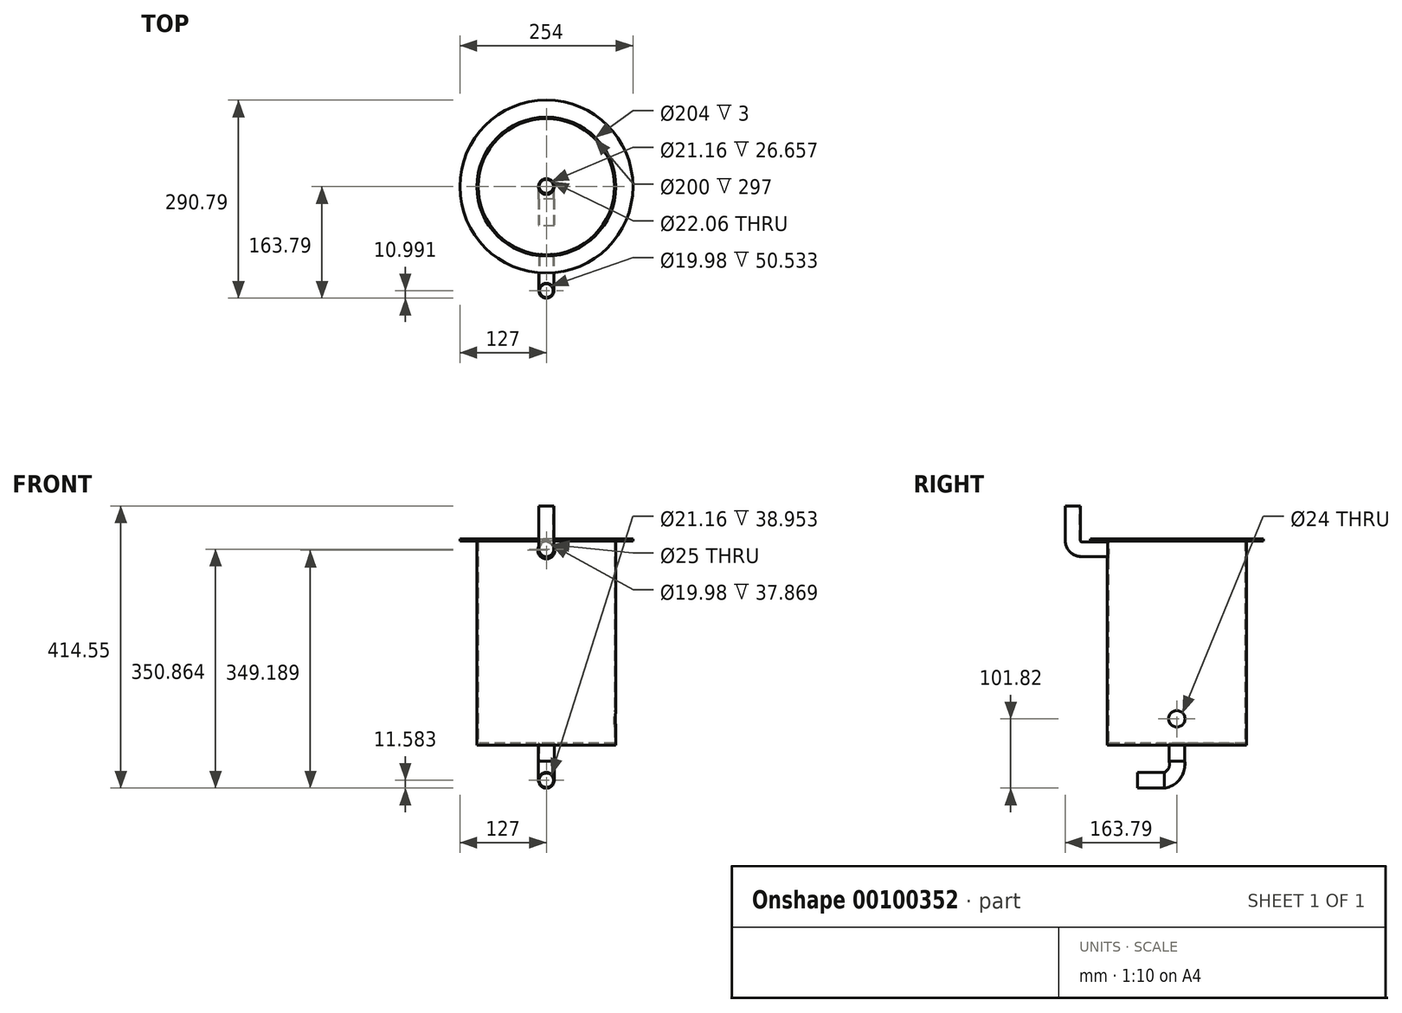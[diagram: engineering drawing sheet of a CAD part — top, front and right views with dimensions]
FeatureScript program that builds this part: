
annotation { "Feature Type Name" : "Feature", "Feature Type Description" : "" }
export const myFeature = defineFeature(function(context is Context, id is Id, definition is map)
    precondition{}
    {
        {
            var Q0;
            Q0=qCreatedBy(makeId("Top.planeOp"),FACE);
            var sketch = newSketch(context, id + "F0", { "sketchPlane" : qUnion([Q0])});
            skCircle(sketch, "E0", {"center": v(0, 0) * mm, "radius": 100 * mm});
            skCircle(sketch, "E1", {"center": v(0, 0) * mm, "radius": 102 * mm});
            skCircle(sketch, "E2", {"center": v(0, 0) * mm, "radius": 11.03 * mm});
            skSolve(sketch);
        }
        {
            var Q0;
            Q0=makeQuery(id+"F0.imprint","IMPRINT",FACE,{"disambiguationData":[TD([[makeQuery(id+"F0.imprint","IMPRINT",EDGE,{"derivedFrom":sQuery(id+"F0.wireOp",EDGE,"E0")}),-1.0]])]});
            extrude(context, id + "F1", {"entities" : qUnion([Q0]), "depth" : 300 * mm});
        }
        {
            var Q0;
            Q0=makeQuery(id+"F1.opExtrude","CAP_FACE",FACE,{"disambiguationData":[OSD([sQuery(id+"F0.wireOp",EDGE,"E0"),sQuery(id+"F0.wireOp",EDGE,"E1")])],"isStart":false});
            var sketch = newSketch(context, id + "F2", { "sketchPlane" : qUnion([Q0])});
            skCircle(sketch, "E3", {"center": v(0, 0) * mm, "radius": 102 * mm});
            skCircle(sketch, "E4", {"center": v(0, 0) * mm, "radius": 127 * mm});
            skSolve(sketch);
        }
        {
            var Q0;
            Q0=makeQuery(id+"F2.imprint","IMPRINT",FACE,{"disambiguationData":[TD([[makeQuery(id+"F2.imprint","IMPRINT",EDGE,{"derivedFrom":sQuery(id+"F2.wireOp",EDGE,"E4")}),1.0]])]});
            var Q1;
            Q1=makeQuery(id+"F2.imprint","IMPRINT",FACE,{"disambiguationData":[TD([[makeQuery(id+"F2.imprint","IMPRINT",EDGE,{"derivedFrom":sQuery(id+"F2.wireOp",EDGE,"E3")}),-1.0]])]});
            extrude(context, id + "F3", {"entities" : qUnion([Q0, Q1]), "depth" : 3 * mm});
        }
        {
            var Q0;
            Q0=qCreatedBy(makeId("Right.planeOp"),FACE);
            cPlane(context, id + "F4", {"entities" : qUnion([Q0]), "cplaneType" : CPlaneType.OFFSET, "offset" : 97 * mm, "width" : 152.4 * mm, "height" : 152.4 * mm});
        }
        {
            var Q0;
            Q0=qCreatedBy(id+"F4.planeOp",FACE);
            var sketch = newSketch(context, id + "F5", { "sketchPlane" : qUnion([Q0])});
            skPoint(sketch, "E5", {"position": v(0, 38.72) * mm});
            skSolve(sketch);
        }
        {
            var Q0;
            Q0=makeQuery(id+"F0.imprint","IMPRINT",FACE,{"disambiguationData":[TD([[makeQuery(id+"F0.imprint","IMPRINT",EDGE,{"derivedFrom":sQuery(id+"F0.wireOp",EDGE,"E0")}),1.0]])]});
            extrude(context, id + "F6", {"entities" : qUnion([Q0]), "operationType" : NewBodyOperationType.ADD, "depth" : 3 * mm});
        }
        {
            var Q0;
            Q0=sQuery(id+"F5.wireOp",VERTEX,"E5");
            var Q1;
            Q1=makeQuery(id+"F1.opExtrude","SWEPT_BODY",BODY,{"disambiguationData":[OSD([sQuery(id+"F0.wireOp",EDGE,"E0"),sQuery(id+"F0.wireOp",EDGE,"E1")])]});
            hole(context, id + "F7", {"style" : HoleStyle.SIMPLE, "endStyle" : HoleEndStyle.BLIND, "oppositeDirection" : true, "holeDiameter" : 24 * mm, "holeDepth" : 30 * mm, "startFromSketch" : true, "locations" : qUnion([Q0]), "scope" : qUnion([Q1])});
        }
        {
            var Q0;
            Q0=qCreatedBy(makeId("Front.planeOp"),FACE);
            cPlane(context, id + "F8", {"entities" : qUnion([Q0]), "cplaneType" : CPlaneType.OFFSET, "offset" : 102 * mm, "width" : 150 * mm, "height" : 150 * mm});
        }
        {
            var Q0;
            Q0=qCreatedBy(id+"F8.planeOp",FACE);
            var sketch = newSketch(context, id + "F9", { "sketchPlane" : qUnion([Q0])});
            skPoint(sketch, "E6", {"position": v(0, 286.09) * mm});
            skSolve(sketch);
        }
        {
            var Q0;
            Q0=sQuery(id+"F9.wireOp",VERTEX,"E6");
            var Q1;
            Q1=makeQuery(id+"F1.opExtrude","SWEPT_BODY",BODY,{"disambiguationData":[OSD([sQuery(id+"F0.wireOp",EDGE,"E0"),sQuery(id+"F0.wireOp",EDGE,"E1")])]});
            hole(context, id + "F10", {"style" : HoleStyle.SIMPLE, "endStyle" : HoleEndStyle.BLIND, "holeDiameter" : 25 * mm, "holeDepth" : 40 * mm, "locations" : qUnion([Q0]), "scope" : qUnion([Q1])});
        }
        {
            var Q0;
            Q0=qCreatedBy(makeId("Right.planeOp"),FACE);
            var sketch = newSketch(context, id + "F11", { "sketchPlane" : qUnion([Q0])});
            skLineSegment(sketch, "E7", {"start": v(-101.77, 287.76) * mm, "end": v(-139.64, 287.76) * mm});
            skArc(sketch, "E8", {"start": v(-139.64, 287.76) * mm, "mid": v(-148.94, 291.62) * mm, "end": v(-152.8, 300.92) * mm});
            skLineSegment(sketch, "E9", {"start": v(-152.8, 300.92) * mm, "end": v(-152.8, 351.45) * mm});
            skSolve(sketch);
        }
        {
            var Q0;
            Q0=qCreatedBy(id+"F8.planeOp",FACE);
            var sketch = newSketch(context, id + "F12", { "sketchPlane" : qUnion([Q0])});
            skCircle(sketch, "E10", {"center": v(0, 287.76) * mm, "radius": 10.99 * mm});
            skCircle(sketch, "E11.0", {"center": v(0, 287.76) * mm, "radius": 9.99 * mm});
            skSolve(sketch);
        }
        {
            var Q0;
            Q0 = qSketchRegion(id + "F12", true);
            var Q1;
            Q1 = qConstructionFilter(qBodyType(qCreatedBy(id + "F11" ,EDGE), BodyType.WIRE), ConstructionObject.NO);
            sweep(context, id + "F13", {"profiles" : qUnion([Q0]), "path" : qUnion([Q1])});
        }
        {
            var Q0;
            Q0=qCreatedBy(makeId("Right.planeOp"),FACE);
            var sketch = newSketch(context, id + "F14", { "sketchPlane" : qUnion([Q0])});
            skArc(sketch, "E12", {"start": v(-0.12, -28.32) * mm, "mid": v(-6.88, -44.64) * mm, "end": v(-23.2, -51.4) * mm});
            skLineSegment(sketch, "E13", {"start": v(-23.2, -51.4) * mm, "end": v(-62.15, -51.4) * mm});
            skLineSegment(sketch, "E14", {"start": v(-0.12, -28.32) * mm, "end": v(-0.12, -1.66) * mm});
            skSolve(sketch);
        }
        {
            var Q0;
            Q0=makeQuery(id+"F6.opExtrude","CAP_FACE",FACE,{"disambiguationData":[OSD([sQuery(id+"F0.wireOp",EDGE,"E0"),sQuery(id+"F0.wireOp",EDGE,"E2")])],"isStart":false});
            var sketch = newSketch(context, id + "F15", { "sketchPlane" : qUnion([Q0])});
            skCircle(sketch, "E15", {"center": v(0, 0) * mm, "radius": 10.58 * mm});
            skCircle(sketch, "E16.0", {"center": v(0, 0) * mm, "radius": 11.58 * mm});
            skSolve(sketch);
        }
        {
            var Q0;
            Q0 = qSketchRegion(id + "F15", true);
            var Q1;
            Q1 = qConstructionFilter(qBodyType(qCreatedBy(id + "F14" ,EDGE), BodyType.WIRE), ConstructionObject.NO);
            sweep(context, id + "F16", {"profiles" : qUnion([Q0]), "path" : qUnion([Q1])});
        }
        {
            var Q0;
            Q0=qCreatedBy(id+"F4.planeOp",FACE);
            var sketch = newSketch(context, id + "F17", { "sketchPlane" : qUnion([Q0])});
            skCircle(sketch, "E17", {"center": v(0, 39) * mm, "radius": 11 * mm});
            skSolve(sketch);
        }
        {
            var Q0;
            Q0=sQuery(id+"F17.wireOp",EDGE,"E17");
            extrude(context, id + "F18", {"bodyType" : ToolBodyType.SURFACE, "surfaceEntities" : qUnion([Q0]), "depth" : 50 * mm});
        }
        {
            var Q0;
            Q0=qCreatedBy(makeId("Top.planeOp"),FACE);
            cPlane(context, id + "F19", {"entities" : qUnion([Q0]), "cplaneType" : CPlaneType.OFFSET, "offset" : 100 * mm, "oppositeDirection" : true, "width" : 150 * mm, "height" : 150 * mm});
        }
        {
            var Q0;
            Q0=qCreatedBy(id+"F19.planeOp",FACE);
            var sketch = newSketch(context, id + "F20", { "sketchPlane" : qUnion([Q0])});
            skLineSegment(sketch, "E18", {"start": v(41.6, -93.05) * mm, "end": v(40.58, -90.68) * mm});
            skLineSegment(sketch, "E19", {"start": v(48.9, 89.43) * mm, "end": v(47.23, 87.4) * mm});
            skLineSegment(sketch, "E20", {"start": v(-44.81, -91.55) * mm, "end": v(-43.6, -89.27) * mm});
            skLineSegment(sketch, "E21", {"start": v(-46.89, 87.59) * mm, "end": v(-48.11, 89.86) * mm});
            skArc(sketch, "E22", {"start": v(40.58, -90.68) * mm, "mid": v(99.28, -3.7) * mm, "end": v(47.23, 87.4) * mm});
            skArc(sketch, "E23", {"start": v(-46.89, 87.59) * mm, "mid": v(-99.33, -1.85) * mm, "end": v(-43.6, -89.27) * mm});
            skArc(sketch, "E24", {"start": v(41.6, -93.05) * mm, "mid": v(101.84, -4.07) * mm, "end": v(48.9, 89.43) * mm});
            skArc(sketch, "E25", {"start": v(-48.11, 89.86) * mm, "mid": v(-101.9, -1.85) * mm, "end": v(-44.81, -91.55) * mm});
            skSolve(sketch);
        }
        {
            var Q0;
            Q0=sQuery(id+"F20.wireOp",EDGE,"E22");
            var Q1;
            Q1=sQuery(id+"F20.wireOp",EDGE,"E24");
            var Q2;
            Q2=sQuery(id+"F20.wireOp",EDGE,"E19");
            var Q3;
            Q3=sQuery(id+"F20.wireOp",EDGE,"E18");
            var Q4;
            Q4=sQuery(id+"F20.wireOp",EDGE,"E25");
            var Q5;
            Q5=sQuery(id+"F20.wireOp",EDGE,"E23");
            var Q6;
            Q6=sQuery(id+"F20.wireOp",EDGE,"E21");
            var Q7;
            Q7=sQuery(id+"F20.wireOp",EDGE,"E20");
            extrude(context, id + "F21", {"bodyType" : ToolBodyType.SURFACE, "surfaceEntities" : qUnion([Q0, Q1, Q2, Q3, Q4, Q5, Q6, Q7]), "depth" : 100 * mm});
        }
    });
